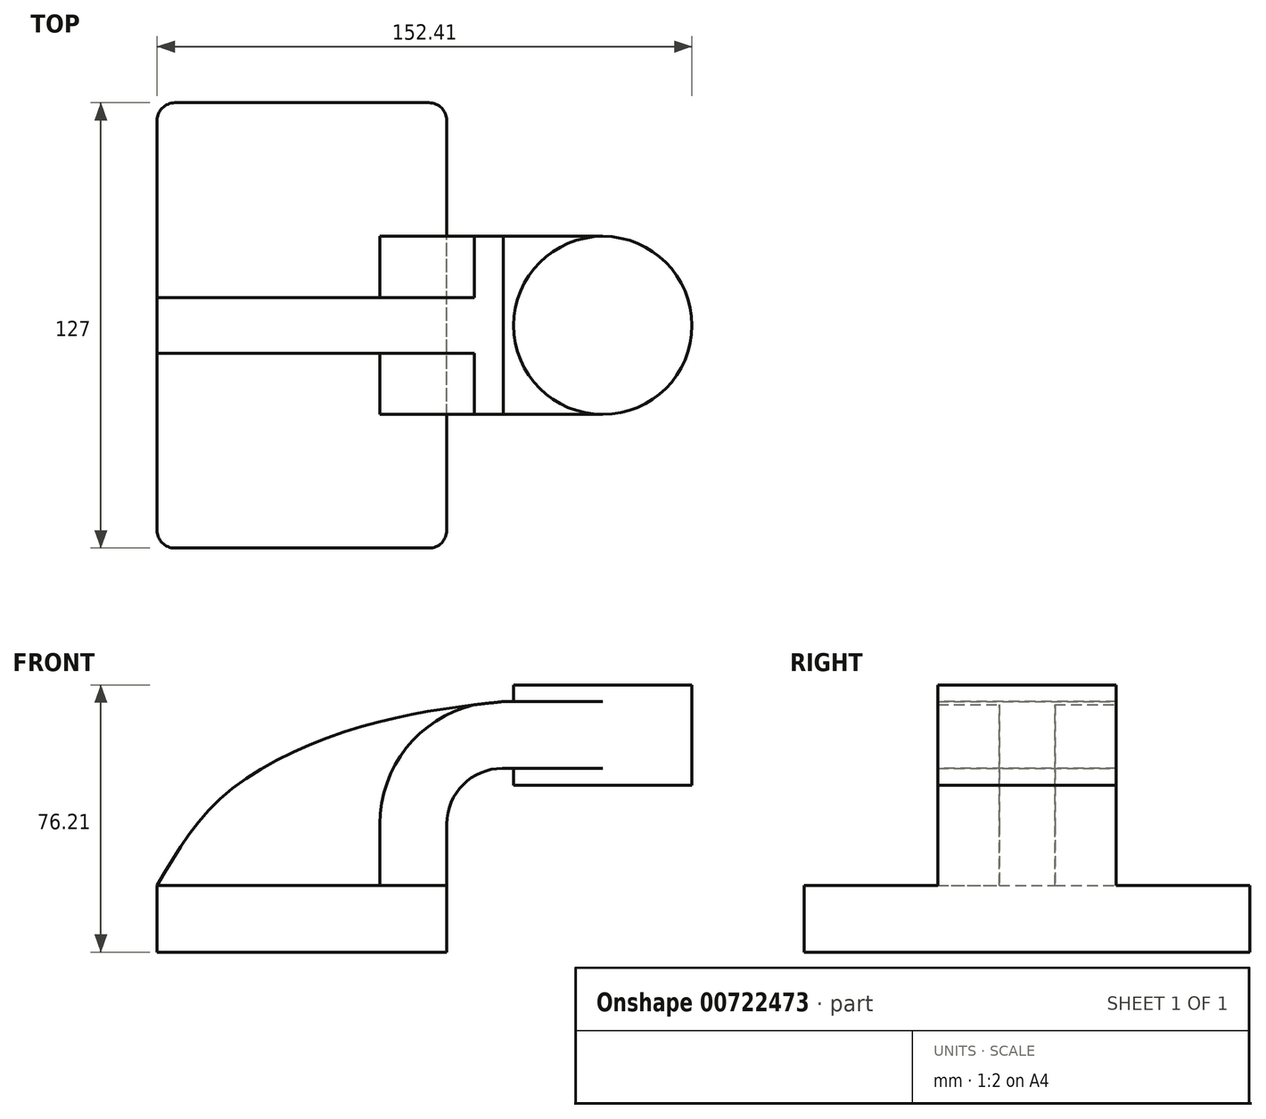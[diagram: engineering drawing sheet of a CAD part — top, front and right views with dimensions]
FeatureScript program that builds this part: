
annotation { "Feature Type Name" : "Feature", "Feature Type Description" : "" }
export const myFeature = defineFeature(function(context is Context, id is Id, definition is map)
    precondition{}
    {
        {
            var Q0;
            Q0=qCreatedBy(makeId("Front.planeOp"),FACE);
            var sketch = newSketch(context, id + "F0", { "sketchPlane" : qUnion([Q0])});
            skLineSegment(sketch, "E0.bottom", {"start": v(41.28, -9.52) * mm, "end": v(-41.27, -9.53) * mm});
            skLineSegment(sketch, "E0.top", {"start": v(41.27, 9.53) * mm, "end": v(-41.28, 9.53) * mm});
            skLineSegment(sketch, "E0.left", {"start": v(41.28, -9.52) * mm, "end": v(41.28, 9.53) * mm});
            skLineSegment(sketch, "E0.right", {"start": v(-41.27, -9.52) * mm, "end": v(-41.28, 9.53) * mm});
            skPoint(sketch, "E0.middle", {"position": v(0, 0) * mm});
            skLineSegment(sketch, "E1.bottom", {"start": v(60.32, 66.68) * mm, "end": v(111.12, 66.68) * mm});
            skLineSegment(sketch, "E1.top", {"start": v(60.33, 38.1) * mm, "end": v(111.12, 38.1) * mm});
            skLineSegment(sketch, "E1.left", {"start": v(60.32, 66.68) * mm, "end": v(60.32, 38.1) * mm});
            skLineSegment(sketch, "E1.right", {"start": v(111.12, 66.68) * mm, "end": v(111.12, 38.1) * mm});
            skPoint(sketch, "E1.middle", {"position": v(85.72, 52.39) * mm});
            skLineSegment(sketch, "E2", {"start": v(41.27, 9.53) * mm, "end": v(41.27, 27) * mm});
            skArc(sketch, "E3", {"start": v(41.27, 27) * mm, "mid": v(45.92, 38.23) * mm, "end": v(57.15, 42.88) * mm});
            skArc(sketch, "E4.0", {"start": v(22.23, 27) * mm, "mid": v(32.52, 51.76) * mm, "end": v(57.34, 61.92) * mm});
            skLineSegment(sketch, "E5", {"start": v(22.23, 27) * mm, "end": v(22.23, 9.53) * mm});
            skFitSpline(sketch, "E6", {"points": [v(-41.28, 9.53) * mm, v(-20.68, 36.41) * mm, v(20.88, 55.87) * mm, v(57.34, 61.92) * mm], "startDerivative": vector(53.79, 92.02) * mm, "endDerivative": vector(107.55, 12) * mm});
            skPoint(sketch, "E7.endSnap0", {"position": v(85.72, 38.1) * mm});
            skLineSegment(sketch, "E8", {"start": v(85.72, 66.68) * mm, "end": v(85.72, 38.1) * mm});
            skLineSegment(sketch, "E9", {"start": v(57.15, 42.88) * mm, "end": v(85.72, 42.88) * mm});
            skLineSegment(sketch, "E10", {"start": v(57.34, 61.92) * mm, "end": v(85.72, 61.92) * mm});
            skSolve(sketch);
        }
        {
            var Q0;
            Q0=makeQuery(id+"F0.imprint","IMPRINT",FACE,{"disambiguationData":[TD([[makeQuery(id+"F0.imprint","IMPRINT",EDGE,{"derivedFrom":sQuery(id+"F0.wireOp",EDGE,"E0.bottom")}),-1.0]])]});
            extrude(context, id + "F1", {"entities" : qUnion([Q0]), "endBound" : BoundingType.SYMMETRIC, "depth" : 127 * mm, "offsetDistance" : 25.4 * mm});
        }
        {
            var Q0;
            {var subQ7=sQuery(id+"F0.wireOp",EDGE,"E2");Q0=makeQuery(id+"F0.imprint","IMPRINT",FACE,{"disambiguationData":[TD([[makeQuery(id+"F0.imprint","IMPRINT",EDGE,{"derivedFrom":subQ7}),1.0]])]});}
            var Q1;
            {var subQ0=sQuery(id+"F0.wireOp",EDGE,"E10");var subQ1=sQuery(id+"F0.wireOp",EDGE,"E1.left");var subQ2=makeQuery(id+"F0.imprint","INTERSECT",VERTEX,{"derivedFrom":[subQ1,subQ0]});Q1=makeQuery(id+"F0.imprint","IMPRINT",FACE,{"disambiguationData":[TD([[makeQuery(id+"F0.imprint","IMPRINT",EDGE,{"disambiguationData":[TD([[subQ2,-1.0]])],"derivedFrom":subQ1}),1.0]])]});}
            extrude(context, id + "F2", {"entities" : qUnion([Q0, Q1]), "operationType" : NewBodyOperationType.ADD, "endBound" : BoundingType.SYMMETRIC, "depth" : 50.8 * mm, "offsetDistance" : 25.4 * mm});
        }
        {
            var Q0;
            {var subQ3=sQuery(id+"F0.wireOp",EDGE,"E5");Q0=makeQuery(id+"F0.imprint","IMPRINT",FACE,{"disambiguationData":[TD([[makeQuery(id+"F0.imprint","IMPRINT",EDGE,{"derivedFrom":subQ3}),-1.0]])]});}
            extrude(context, id + "F3", {"entities" : qUnion([Q0]), "operationType" : NewBodyOperationType.ADD, "endBound" : BoundingType.SYMMETRIC, "depth" : 15.88 * mm, "offsetDistance" : 25.4 * mm});
        }
        {
            var Q0;
            {var subQ4=sQuery(id+"F0.wireOp",EDGE,"E1.right");Q0=makeQuery(id+"F0.imprint","IMPRINT",FACE,{"disambiguationData":[TD([[makeQuery(id+"F0.imprint","IMPRINT",EDGE,{"derivedFrom":subQ4}),-1.0]])]});}
            var Q1;
            Q1=sQuery(id+"F0.wireOp",EDGE,"E8");
            revolve(context, id + "F4", {"operationType" : NewBodyOperationType.ADD, "surfaceOperationType" : NewSurfaceOperationType.NEW, "entities" : qUnion([Q0]), "axis" : qUnion([Q1]), "revolveType" : RevolveType.FULL});
        }
        {
            var Q0;
            Q0=makeQuery(id+"F1.opExtrude","CAP_EDGE",EDGE,{"disambiguationData":[OSD([sQuery(id+"F0.wireOp",EDGE,"E0.left")])],"isStart":false});
            var Q1;
            Q1=makeQuery(id+"F1.opExtrude","CAP_EDGE",EDGE,{"disambiguationData":[OSD([sQuery(id+"F0.wireOp",EDGE,"E0.right")])],"isStart":false});
            var Q2;
            Q2=makeQuery(id+"F1.opExtrude","CAP_EDGE",EDGE,{"disambiguationData":[OSD([sQuery(id+"F0.wireOp",EDGE,"E0.right")])],"isStart":true});
            var Q3;
            Q3=makeQuery(id+"F1.opExtrude","CAP_EDGE",EDGE,{"disambiguationData":[OSD([sQuery(id+"F0.wireOp",EDGE,"E0.left")])],"isStart":true});
            fillet(context, id + "F5", {"entities" : qUnion([Q0, Q1, Q2, Q3]), "radius" : 5.08 * mm, "tangentPropagation" : true, "allowEdgeOverflow" : false});
        }
    });
